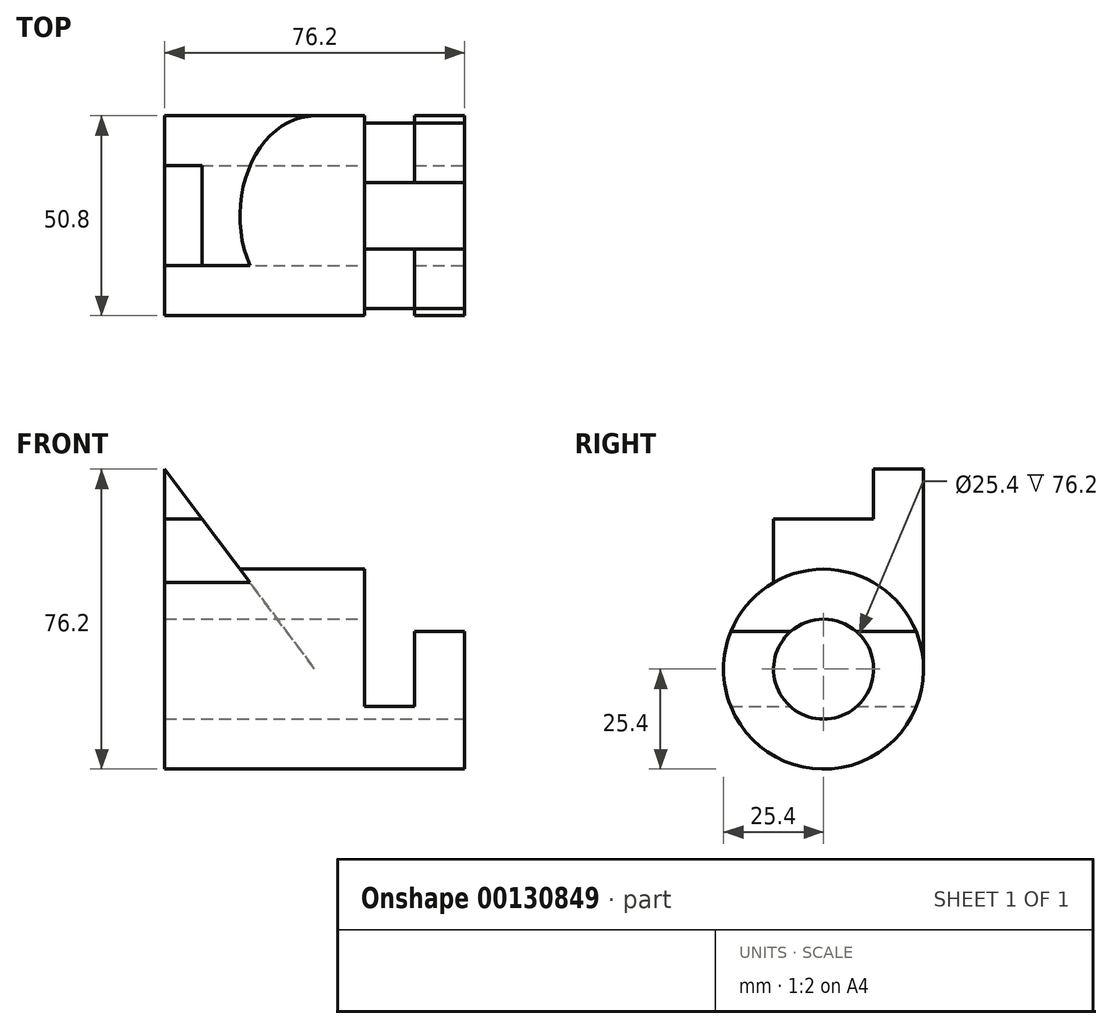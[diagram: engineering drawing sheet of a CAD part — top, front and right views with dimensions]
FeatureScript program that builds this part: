
annotation { "Feature Type Name" : "Feature", "Feature Type Description" : "" }
export const myFeature = defineFeature(function(context is Context, id is Id, definition is map)
    precondition{}
    {
        {
            var Q0;
            Q0=qCreatedBy(makeId("Right.planeOp"),FACE);
            var sketch = newSketch(context, id + "F0", { "sketchPlane" : qUnion([Q0])});
            skLineSegment(sketch, "E0", {"start": v(0, 0) * mm, "end": v(0, 50.8) * mm});
            skLineSegment(sketch, "E1", {"start": v(0, 50.8) * mm, "end": v(-12.7, 50.8) * mm});
            skLineSegment(sketch, "E2", {"start": v(-12.7, 50.8) * mm, "end": v(-12.7, 38.1) * mm});
            skLineSegment(sketch, "E3", {"start": v(-12.7, 38.1) * mm, "end": v(-38.1, 38.1) * mm});
            skLineSegment(sketch, "E4", {"start": v(-38.1, 38.1) * mm, "end": v(-38.1, 0) * mm});
            skLineSegment(sketch, "E5", {"start": v(-38.1, 0) * mm, "end": v(0, 0) * mm});
            skSolve(sketch);
        }
        {
            var Q0;
            Q0 = qSketchRegion(id + "F0", true);
            extrude(context, id + "F1", {"entities" : qUnion([Q0]), "oppositeDirection" : true, "depth" : 38.1 * mm});
        }
        {
            var Q0;
            Q0=qCreatedBy(makeId("Front.planeOp"),FACE);
            var sketch = newSketch(context, id + "F2", { "sketchPlane" : qUnion([Q0])});
            skLineSegment(sketch, "E6", {"start": v(0, 0) * mm, "end": v(-38.1, 50.8) * mm});
            skLineSegment(sketch, "E7", {"start": v(-38.1, 50.8) * mm, "end": v(0, 50.8) * mm});
            skLineSegment(sketch, "E8", {"start": v(0, 50.8) * mm, "end": v(0, 0) * mm});
            skSolve(sketch);
        }
        {
            var Q0;
            Q0 = qSketchRegion(id + "F2", true);
            extrude(context, id + "F3", {"entities" : qUnion([Q0]), "operationType" : NewBodyOperationType.REMOVE, "endBound" : BoundingType.THROUGH_ALL, "depth" : 25.4 * mm});
        }
        {
            var Q0;
            Q0=qCreatedBy(makeId("Right.planeOp"),FACE);
            cPlane(context, id + "F4", {"entities" : qUnion([Q0]), "cplaneType" : CPlaneType.OFFSET, "offset" : 12.7 * mm, "width" : 152.4 * mm, "height" : 152.4 * mm});
        }
        {
            var Q0;
            Q0=qCreatedBy(id+"F4.planeOp",FACE);
            var sketch = newSketch(context, id + "F5", { "sketchPlane" : qUnion([Q0])});
            skLineSegment(sketch, "E9", {"start": v(0, 0) * mm, "end": v(-25.4, 0) * mm, "construction": true});
            skCircle(sketch, "E10", {"center": v(-25.4, 0) * mm, "radius": 25.4 * mm});
            skSolve(sketch);
        }
        {
            var Q0;
            Q0 = qSketchRegion(id + "F5", true);
            extrude(context, id + "F6", {"entities" : qUnion([Q0]), "operationType" : NewBodyOperationType.ADD, "oppositeDirection" : true, "depth" : 50.8 * mm});
        }
        {
            var Q0;
            Q0=makeQuery(id+"F6.opExtrude","CAP_FACE",FACE,{"disambiguationData":[OSD([sQuery(id+"F5.wireOp",EDGE,"E10")])],"isStart":true});
            extrude(context, id + "F7", {"entities" : qUnion([Q0]), "operationType" : NewBodyOperationType.ADD, "depth" : 25.4 * mm});
        }
        {
            var Q0;
            Q0=makeQuery(id+"F7.opExtrude","CAP_FACE",FACE,{"disambiguationData":[OSD([sQuery(id+"F5.wireOp",EDGE,"E10")])],"isStart":false});
            var sketch = newSketch(context, id + "F8", { "sketchPlane" : qUnion([Q0])});
            skCircle(sketch, "E11", {"center": v(-25.4, 0) * mm, "radius": 12.7 * mm});
            skSolve(sketch);
        }
        {
            var Q0;
            Q0 = qSketchRegion(id + "F8", true);
            extrude(context, id + "F9", {"entities" : qUnion([Q0]), "operationType" : NewBodyOperationType.REMOVE, "endBound" : BoundingType.THROUGH_ALL, "oppositeDirection" : true, "depth" : 25.4 * mm});
        }
        {
            var Q0;
            Q0=qCreatedBy(makeId("Front.planeOp"),FACE);
            var sketch = newSketch(context, id + "F10", { "sketchPlane" : qUnion([Q0])});
            skLineSegment(sketch, "E12", {"start": v(38.1, 25.4) * mm, "end": v(38.1, 9.53) * mm});
            skLineSegment(sketch, "E13", {"start": v(38.1, 9.53) * mm, "end": v(25.4, 9.52) * mm});
            skLineSegment(sketch, "E14", {"start": v(25.4, 9.52) * mm, "end": v(25.4, -9.52) * mm});
            skLineSegment(sketch, "E15", {"start": v(25.4, -9.52) * mm, "end": v(12.7, -9.52) * mm});
            skLineSegment(sketch, "E16", {"start": v(12.7, -9.52) * mm, "end": v(12.7, 25.4) * mm});
            skLineSegment(sketch, "E17", {"start": v(12.7, 25.4) * mm, "end": v(12.7, 0) * mm});
            skLineSegment(sketch, "E18", {"start": v(12.7, 0) * mm, "end": v(12.7, -9.52) * mm});
            skLineSegment(sketch, "E19", {"start": v(12.7, 25.4) * mm, "end": v(38.1, 25.4) * mm});
            skSolve(sketch);
        }
        {
            var Q0;
            Q0 = qSketchRegion(id + "F10", true);
            extrude(context, id + "F11", {"entities" : qUnion([Q0]), "operationType" : NewBodyOperationType.REMOVE, "endBound" : BoundingType.THROUGH_ALL, "depth" : 25.4 * mm});
        }
    });
